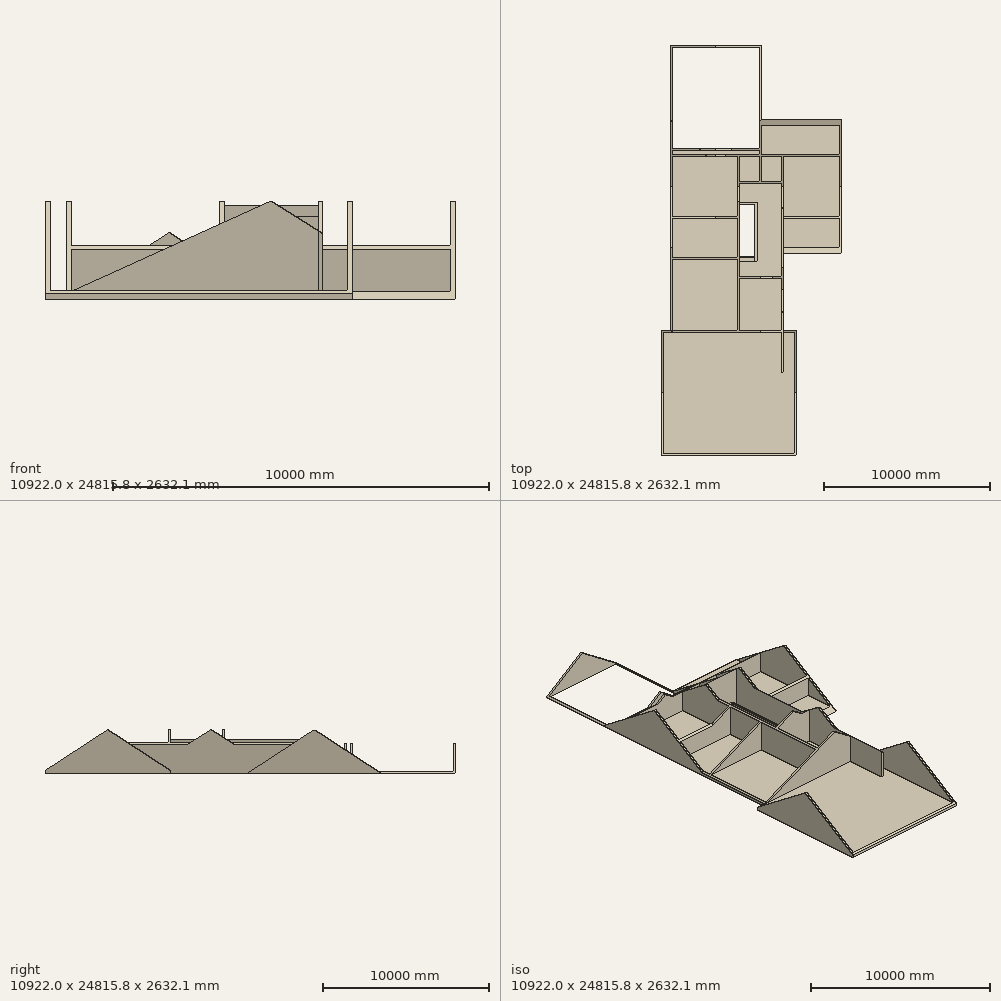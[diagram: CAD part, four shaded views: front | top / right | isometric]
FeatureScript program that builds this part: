
annotation { "Feature Type Name" : "Feature", "Feature Type Description" : "" }
export const myFeature = defineFeature(function(context is Context, id is Id, definition is map)
    precondition{}
    {
        {
            var Q0;
            Q0=qCreatedBy(makeId("Top.planeOp"),FACE);
            var sketch = newSketch(context, id + "F0", { "sketchPlane" : qUnion([Q0])});
            skLineSegment(sketch, "E0", {"start": v(0, 0) * mm, "end": v(8178.8, 0) * mm});
            skLineSegment(sketch, "E1", {"start": v(0, 0) * mm, "end": v(0, 7569.2) * mm});
            skLineSegment(sketch, "E2", {"start": v(0, 7569.2) * mm, "end": v(558.8, 7569.2) * mm});
            skLineSegment(sketch, "E3", {"start": v(558.8, 7569.2) * mm, "end": v(558.8, 24815.8) * mm});
            skLineSegment(sketch, "E4", {"start": v(558.8, 24815.8) * mm, "end": v(6045.2, 24815.8) * mm});
            skLineSegment(sketch, "E5", {"start": v(6045.2, 24815.8) * mm, "end": v(6045.2, 20548.6) * mm});
            skLineSegment(sketch, "E6", {"start": v(6045.2, 20548.6) * mm, "end": v(10922, 20548.6) * mm});
            skLineSegment(sketch, "E7", {"start": v(10922, 20548.6) * mm, "end": v(10922, 12014.2) * mm});
            skLineSegment(sketch, "E8", {"start": v(10922, 12014.2) * mm, "end": v(7391.4, 12014.2) * mm});
            skLineSegment(sketch, "E9", {"start": v(7391.4, 12014.2) * mm, "end": v(7391.4, 7569.2) * mm});
            skLineSegment(sketch, "E10", {"start": v(7391.4, 7569.2) * mm, "end": v(8178.8, 7569.2) * mm});
            skLineSegment(sketch, "E11", {"start": v(8178.8, 7569.2) * mm, "end": v(8178.8, 0) * mm});
            skSolve(sketch);
        }
        {
            var Q0;
            Q0 = qSketchRegion(id + "F0", true);
            extrude(context, id + "F1", {"entities" : qUnion([Q0]), "depth" : 2632.07 * mm});
        }
        {
            var Q0;
            Q0=makeQuery(id+"F1.opExtrude","SWEPT_FACE",FACE,{"disambiguationData":[OSD([sQuery(id+"F0.wireOp",EDGE,"E7")])]});
            var sketch = newSketch(context, id + "F2", { "sketchPlane" : qUnion([Q0])});
            skLineSegment(sketch, "E12", {"start": v(16281.4, 2632.08) * mm, "end": v(16281.4, 219.08) * mm, "construction": true});
            skLineSegment(sketch, "E13", {"start": v(14452.6, 219.08) * mm, "end": v(18110.2, 219.08) * mm, "construction": true});
            skLineSegment(sketch, "E14", {"start": v(14452.6, 219.08) * mm, "end": v(14452.6, 1438.28) * mm, "construction": true});
            skLineSegment(sketch, "E15", {"start": v(16281.4, 2632.08) * mm, "end": v(12249.29, 0) * mm});
            skLineSegment(sketch, "E16", {"start": v(12249.29, 0) * mm, "end": v(12014.2, 0) * mm});
            skLineSegment(sketch, "E17", {"start": v(12014.2, 0) * mm, "end": v(12014.2, 2632.08) * mm});
            skLineSegment(sketch, "E18", {"start": v(12014.2, 2632.08) * mm, "end": v(16281.4, 2632.08) * mm});
            skLineSegment(sketch, "E19.MirrorCS", {"start": v(16281.4, 2632.08) * mm, "end": v(20313.51, 0) * mm});
            skLineSegment(sketch, "E20.MirrorCS", {"start": v(20313.51, 0) * mm, "end": v(20548.6, 0) * mm});
            skLineSegment(sketch, "E21.MirrorCS", {"start": v(20548.6, 0) * mm, "end": v(20548.6, 2632.08) * mm});
            skLineSegment(sketch, "E22.MirrorCS", {"start": v(20548.6, 2632.08) * mm, "end": v(16281.4, 2632.08) * mm});
            skLineSegment(sketch, "E23", {"start": v(3784.6, 2632.08) * mm, "end": v(3784.6, 219.08) * mm, "construction": true});
            skLineSegment(sketch, "E24", {"start": v(1955.8, 219.08) * mm, "end": v(5613.4, 219.08) * mm, "construction": true});
            skLineSegment(sketch, "E25", {"start": v(1955.8, 219.08) * mm, "end": v(1955.8, 1438.28) * mm, "construction": true});
            skLineSegment(sketch, "E26", {"start": v(3784.6, 2632.08) * mm, "end": v(0, 161.57) * mm});
            skLineSegment(sketch, "E27", {"start": v(0, 161.57) * mm, "end": v(0, 2632.08) * mm});
            skLineSegment(sketch, "E28", {"start": v(0, 2632.08) * mm, "end": v(3784.6, 2632.08) * mm});
            skLineSegment(sketch, "E29.MirrorCS", {"start": v(3784.6, 2632.08) * mm, "end": v(7569.2, 161.57) * mm});
            skLineSegment(sketch, "E30.MirrorCS", {"start": v(7569.2, 161.57) * mm, "end": v(7569.2, 2632.08) * mm});
            skLineSegment(sketch, "E31.MirrorCS", {"start": v(7569.2, 2632.08) * mm, "end": v(3784.6, 2632.08) * mm});
            skSolve(sketch);
        }
        {
            var Q0;
            Q0 = qSketchRegion(id + "F2", true);
            var Q1;
            Q1=makeQuery(id+"F1.opExtrude","SWEPT_FACE",FACE,{"disambiguationData":[OSD([sQuery(id+"F0.wireOp",EDGE,"E1")])]});
            extrude(context, id + "F3", {"entities" : qUnion([Q0]), "operationType" : NewBodyOperationType.REMOVE, "endBound" : BoundingType.UP_TO_SURFACE, "oppositeDirection" : true, "endBoundEntityFace" : qUnion([Q1]), "depth" : 25.4 * mm});
        }
        {
            var Q0;
            Q0=makeQuery(id+"F3.boolean.opBoolean","COPY",FACE,{"derivedFrom":makeQuery(id+"F3.opExtrude","SWEPT_FACE",FACE,{"disambiguationData":[OSD([sQuery(id+"F2.wireOp",EDGE,"E30.MirrorCS")])]})});
            var sketch = newSketch(context, id + "F4", { "sketchPlane" : qUnion([Q0])});
            skLineSegment(sketch, "E32", {"start": v(6010.27, 2632.07) * mm, "end": v(6010.27, 219.07) * mm, "construction": true});
            skLineSegment(sketch, "E33", {"start": v(4756.15, 219.07) * mm, "end": v(7264.4, 219.07) * mm, "construction": true});
            skLineSegment(sketch, "E34", {"start": v(4756.15, 219.07) * mm, "end": v(4756.15, 1844.67) * mm, "construction": true});
            skLineSegment(sketch, "E35", {"start": v(6010.27, 2632.07) * mm, "end": v(558.8, 161.57) * mm});
            skLineSegment(sketch, "E36", {"start": v(558.8, 161.57) * mm, "end": v(558.8, 2632.07) * mm});
            skLineSegment(sketch, "E37", {"start": v(558.8, 2632.07) * mm, "end": v(6010.27, 2632.07) * mm});
            skLineSegment(sketch, "E38.MirrorCS", {"start": v(7264.4, 219.07) * mm, "end": v(7264.4, 1844.67) * mm, "construction": true});
            skLineSegment(sketch, "E39", {"start": v(6010.27, 2632.07) * mm, "end": v(7391.4, 1764.94) * mm});
            skLineSegment(sketch, "E40", {"start": v(7391.4, 1764.94) * mm, "end": v(7391.4, 2632.07) * mm});
            skLineSegment(sketch, "E41", {"start": v(7391.4, 2632.07) * mm, "end": v(6010.27, 2632.07) * mm});
            skSolve(sketch);
        }
        {
            var Q0;
            Q0 = qSketchRegion(id + "F4", true);
            extrude(context, id + "F5", {"entities" : qUnion([Q0]), "operationType" : NewBodyOperationType.REMOVE, "endBound" : BoundingType.UP_TO_NEXT, "oppositeDirection" : true, "depth" : 25.4 * mm});
        }
        {
            var Q0;
            Q0=makeQuery(id+"F3.boolean.opBoolean","COPY",FACE,{"derivedFrom":makeQuery(id+"F3.opExtrude","SWEPT_FACE",FACE,{"disambiguationData":[OSD([sQuery(id+"F2.wireOp",EDGE,"E30.MirrorCS")])]})});
            var sketch = newSketch(context, id + "F6", { "sketchPlane" : qUnion([Q0])});
            skLineSegment(sketch, "E42", {"start": v(558.8, 161.57) * mm, "end": v(6010.27, 2632.08) * mm});
            skLineSegment(sketch, "E43", {"start": v(6010.27, 2632.08) * mm, "end": v(7391.4, 1764.94) * mm});
            skLineSegment(sketch, "E44", {"start": v(7391.4, 1764.94) * mm, "end": v(7391.4, 161.57) * mm});
            skLineSegment(sketch, "E45", {"start": v(7391.4, 161.57) * mm, "end": v(558.8, 161.57) * mm});
            skSolve(sketch);
        }
        {
            var Q0;
            Q0 = qSketchRegion(id + "F6", true);
            extrude(context, id + "F7", {"entities" : qUnion([Q0]), "operationType" : NewBodyOperationType.ADD, "endBound" : BoundingType.UP_TO_NEXT, "depth" : 25.4 * mm});
        }
        {
            var Q0;
            Q0=makeQuery(id+"F3.boolean.opBoolean","COPY",FACE,{"derivedFrom":makeQuery(id+"F3.opExtrude","SWEPT_FACE",FACE,{"disambiguationData":[OSD([sQuery(id+"F2.wireOp",EDGE,"E17")])]})});
            var sketch = newSketch(context, id + "F8", { "sketchPlane" : qUnion([Q0])});
            skLineSegment(sketch, "E46", {"start": v(-6010.27, 2632.08) * mm, "end": v(-7391.4, 1764.94) * mm});
            skLineSegment(sketch, "E47", {"start": v(-7391.4, 1764.94) * mm, "end": v(-7391.4, 0) * mm});
            skLineSegment(sketch, "E48", {"start": v(-7391.4, 0) * mm, "end": v(-558.8, 0) * mm});
            skLineSegment(sketch, "E49", {"start": v(-558.8, 161.57) * mm, "end": v(-6010.27, 2632.08) * mm});
            skLineSegment(sketch, "E50", {"start": v(-558.8, 161.57) * mm, "end": v(-558.8, 0) * mm});
            skSolve(sketch);
        }
        {
            var Q0;
            Q0 = qSketchRegion(id + "F8", true);
            extrude(context, id + "F9", {"entities" : qUnion([Q0]), "operationType" : NewBodyOperationType.ADD, "endBound" : BoundingType.UP_TO_NEXT, "depth" : 25.4 * mm});
        }
        {
            var Q0;
            Q0=makeQuery(id+"F1.opExtrude","SWEPT_FACE",FACE,{"disambiguationData":[OSD([sQuery(id+"F0.wireOp",EDGE,"E4")])]});
            var sketch = newSketch(context, id + "F10", { "sketchPlane" : qUnion([Q0])});
            skLineSegment(sketch, "E51", {"start": v(-3302, 2632.08) * mm, "end": v(-3302, 0) * mm, "construction": true});
            skPoint(sketch, "E52", {"position": v(-3302, 219.07) * mm});
            skPoint(sketch, "E53", {"position": v(-3302, 1793.88) * mm});
            skLineSegment(sketch, "E54", {"start": v(-5130.8, 219.07) * mm, "end": v(-1473.2, 219.07) * mm, "construction": true});
            skLineSegment(sketch, "E55", {"start": v(-5130.8, 219.08) * mm, "end": v(-5130.8, 1438.27) * mm, "construction": true});
            skLineSegment(sketch, "E56", {"start": v(-5130.8, 1438.27) * mm, "end": v(-3302, 2632.08) * mm, "construction": true});
            skLineSegment(sketch, "E57", {"start": v(-3302, 1793.88) * mm, "end": v(-6045.2, 3.17) * mm});
            skLineSegment(sketch, "E58", {"start": v(-6045.2, 3.17) * mm, "end": v(-6045.2, 2632.08) * mm});
            skLineSegment(sketch, "E59", {"start": v(-6045.2, 2632.08) * mm, "end": v(-3302, 2632.08) * mm});
            skLineSegment(sketch, "E60.MirrorCS", {"start": v(-3302, 1793.88) * mm, "end": v(-558.8, 3.17) * mm});
            skLineSegment(sketch, "E61.MirrorCS", {"start": v(-558.8, 3.17) * mm, "end": v(-558.8, 2632.08) * mm});
            skLineSegment(sketch, "E62.MirrorCS", {"start": v(-558.8, 2632.08) * mm, "end": v(-3302, 2632.08) * mm});
            skSolve(sketch);
        }
        {
            var Q0;
            Q0 = qSketchRegion(id + "F10", true);
            extrude(context, id + "F11", {"entities" : qUnion([Q0]), "operationType" : NewBodyOperationType.REMOVE, "endBound" : BoundingType.UP_TO_NEXT, "oppositeDirection" : true, "depth" : 25.4 * mm});
        }
        {
            var Q0;
            Q0=makeQuery(id+"F3.boolean.opBoolean","COPY",FACE,{"derivedFrom":makeQuery(id+"F3.opExtrude","SWEPT_FACE",FACE,{"disambiguationData":[OSD([sQuery(id+"F2.wireOp",EDGE,"E21.MirrorCS")])]})});
            var sketch = newSketch(context, id + "F12", { "sketchPlane" : qUnion([Q0])});
            skLineSegment(sketch, "E63", {"start": v(3302, 1793.88) * mm, "end": v(558.8, 3.17) * mm});
            skLineSegment(sketch, "E64", {"start": v(558.8, 3.17) * mm, "end": v(558.8, 0) * mm});
            skLineSegment(sketch, "E65", {"start": v(558.8, 0) * mm, "end": v(6045.2, 0) * mm});
            skLineSegment(sketch, "E66", {"start": v(6045.2, 0) * mm, "end": v(6045.2, 3.17) * mm});
            skLineSegment(sketch, "E67", {"start": v(6045.2, 3.17) * mm, "end": v(3302, 1793.88) * mm});
            skSolve(sketch);
        }
        {
            var Q0;
            Q0 = qSketchRegion(id + "F12", true);
            extrude(context, id + "F13", {"entities" : qUnion([Q0]), "operationType" : NewBodyOperationType.ADD, "endBound" : BoundingType.UP_TO_NEXT, "depth" : 25.4 * mm});
        }
        {
            var Q0;
            Q0=makeQuery(id+"F9.boolean.opBoolean","MERGE",FACE,{"derivedFrom":[makeQuery(id+"F7.boolean.opBoolean","MERGE",FACE,{"derivedFrom":[makeQuery(id+"F1.opExtrude","SWEPT_FACE",FACE,{"disambiguationData":[OSD([sQuery(id+"F0.wireOp",EDGE,"E9")])]}),makeQuery(id+"F7.opExtrude","SWEPT_FACE",FACE,{"disambiguationData":[OSD([sQuery(id+"F6.wireOp",EDGE,"E44")])]})]}),makeQuery(id+"F9.opExtrude","SWEPT_FACE",FACE,{"disambiguationData":[OSD([sQuery(id+"F8.wireOp",EDGE,"E47")])]})]});
            var sketch = newSketch(context, id + "F14", { "sketchPlane" : qUnion([Q0])});
            skLineSegment(sketch, "E68", {"start": v(3784.6, 2632.08) * mm, "end": v(16281.4, 2632.08) * mm, "construction": true});
            skLineSegment(sketch, "E69", {"start": v(10033, 2632.08) * mm, "end": v(10033, 0) * mm, "construction": true});
            skLineSegment(sketch, "E70", {"start": v(8778.88, 219.08) * mm, "end": v(11287.13, 219.08) * mm, "construction": true});
            skPoint(sketch, "E71", {"position": v(10033, 219.08) * mm});
            skLineSegment(sketch, "E72", {"start": v(8778.88, 219.08) * mm, "end": v(8778.88, 1844.68) * mm, "construction": true});
            skLineSegment(sketch, "E73", {"start": v(10033, 2632.07) * mm, "end": v(8651.87, 1764.94) * mm});
            skLineSegment(sketch, "E74.MirrorCS", {"start": v(10033, 2632.07) * mm, "end": v(11414.13, 1764.94) * mm});
            skLineSegment(sketch, "E75", {"start": v(8651.87, 1764.94) * mm, "end": v(11414.13, 1764.94) * mm});
            skSolve(sketch);
        }
        {
            var Q0;
            Q0 = qSketchRegion(id + "F14", true);
            extrude(context, id + "F15", {"entities" : qUnion([Q0]), "operationType" : NewBodyOperationType.ADD, "endBound" : BoundingType.UP_TO_NEXT, "oppositeDirection" : true, "depth" : 25.4 * mm});
        }
        {
            var Q0;
            Q0=qCreatedBy(makeId("Top.planeOp"),FACE);
            cPlane(context, id + "F16", {"entities" : qUnion([Q0]), "cplaneType" : CPlaneType.OFFSET, "offset" : 2632.07 * mm, "width" : 152.4 * mm, "height" : 152.4 * mm});
        }
        {
            var Q0;
            Q0=qCreatedBy(id+"F16.planeOp",FACE);
            var sketch = newSketch(context, id + "F17", { "sketchPlane" : qUnion([Q0])});
            skLineSegment(sketch, "E76.bottom", {"start": v(685.8, 24688.8) * mm, "end": v(5918.2, 24688.8) * mm});
            skLineSegment(sketch, "E76.top", {"start": v(685.8, 18592.8) * mm, "end": v(5918.2, 18592.8) * mm});
            skLineSegment(sketch, "E76.left", {"start": v(685.8, 24688.8) * mm, "end": v(685.8, 18592.8) * mm});
            skLineSegment(sketch, "E76.right", {"start": v(5918.2, 24688.8) * mm, "end": v(5918.2, 18592.8) * mm});
            skSolve(sketch);
        }
        {
            var Q0;
            Q0 = qSketchRegion(id + "F17", true);
            extrude(context, id + "F18", {"entities" : qUnion([Q0]), "operationType" : NewBodyOperationType.REMOVE, "endBound" : BoundingType.THROUGH_ALL, "oppositeDirection" : true, "depth" : 25.4 * mm});
        }
        {
            var Q0;
            Q0=qCreatedBy(id+"F16.planeOp",FACE);
            var sketch = newSketch(context, id + "F19", { "sketchPlane" : qUnion([Q0])});
            skLineSegment(sketch, "E77.bottom", {"start": v(7391.4, 18110.2) * mm, "end": v(10795, 18110.2) * mm});
            skLineSegment(sketch, "E77.top", {"start": v(7391.4, 14452.6) * mm, "end": v(10795, 14452.6) * mm});
            skLineSegment(sketch, "E77.left", {"start": v(7391.4, 18110.2) * mm, "end": v(7391.4, 14452.6) * mm});
            skLineSegment(sketch, "E77.right", {"start": v(10795, 18110.2) * mm, "end": v(10795, 14452.6) * mm});
            skLineSegment(sketch, "E78", {"start": v(10922, 16281.4) * mm, "end": v(558.8, 16281.4) * mm, "construction": true});
            skPoint(sketch, "E79", {"position": v(10795, 16281.4) * mm});
            skLineSegment(sketch, "E80.bottom", {"start": v(685.8, 18110.2) * mm, "end": v(4629.15, 18110.2) * mm});
            skLineSegment(sketch, "E80.top", {"start": v(685.8, 14452.6) * mm, "end": v(4629.15, 14452.6) * mm});
            skLineSegment(sketch, "E80.left", {"start": v(685.8, 18110.2) * mm, "end": v(685.8, 14452.6) * mm});
            skLineSegment(sketch, "E80.right", {"start": v(4629.15, 18110.2) * mm, "end": v(4629.15, 14452.6) * mm});
            skLineSegment(sketch, "E81.bottom", {"start": v(4756.15, 18110.2) * mm, "end": v(5946.77, 18110.2) * mm});
            skLineSegment(sketch, "E81.top", {"start": v(4756.15, 16586.2) * mm, "end": v(5946.77, 16586.2) * mm});
            skLineSegment(sketch, "E81.left", {"start": v(4756.15, 18110.2) * mm, "end": v(4756.15, 16586.2) * mm});
            skLineSegment(sketch, "E81.right", {"start": v(5946.77, 18110.2) * mm, "end": v(5946.77, 16586.2) * mm});
            skLineSegment(sketch, "E82.bottom", {"start": v(7264.4, 18110.2) * mm, "end": v(6073.77, 18110.2) * mm});
            skLineSegment(sketch, "E82.top", {"start": v(7264.4, 16586.2) * mm, "end": v(6073.77, 16586.2) * mm});
            skLineSegment(sketch, "E82.left", {"start": v(7264.4, 18110.2) * mm, "end": v(7264.4, 16586.2) * mm});
            skLineSegment(sketch, "E82.right", {"start": v(6073.77, 18110.2) * mm, "end": v(6073.77, 16586.2) * mm});
            skLineSegment(sketch, "E83.bottom", {"start": v(10795, 14325.6) * mm, "end": v(7391.4, 14325.6) * mm});
            skLineSegment(sketch, "E83.top", {"start": v(10795, 12014.2) * mm, "end": v(7391.4, 12014.2) * mm});
            skLineSegment(sketch, "E83.left", {"start": v(10795, 14325.6) * mm, "end": v(10795, 12014.2) * mm});
            skLineSegment(sketch, "E83.right", {"start": v(7391.4, 14325.6) * mm, "end": v(7391.4, 12014.2) * mm});
            skLineSegment(sketch, "E84.bottom", {"start": v(10795, 18237.2) * mm, "end": v(6045.2, 18237.2) * mm});
            skLineSegment(sketch, "E84.top", {"start": v(10795, 20548.6) * mm, "end": v(6045.2, 20548.6) * mm});
            skLineSegment(sketch, "E84.left", {"start": v(10795, 18237.2) * mm, "end": v(10795, 20548.6) * mm});
            skLineSegment(sketch, "E84.right", {"start": v(6045.2, 18237.2) * mm, "end": v(6045.2, 20548.6) * mm});
            skLineSegment(sketch, "E85.bottom", {"start": v(685.8, 18237.2) * mm, "end": v(5918.2, 18237.2) * mm});
            skLineSegment(sketch, "E85.top", {"start": v(685.8, 18465.8) * mm, "end": v(5918.2, 18465.8) * mm});
            skLineSegment(sketch, "E85.left", {"start": v(685.8, 18237.2) * mm, "end": v(685.8, 18465.8) * mm});
            skLineSegment(sketch, "E85.right", {"start": v(5918.2, 18237.2) * mm, "end": v(5918.2, 18465.8) * mm});
            skLineSegment(sketch, "E86.bottom", {"start": v(685.8, 14325.6) * mm, "end": v(4629.15, 14325.6) * mm});
            skLineSegment(sketch, "E86.top", {"start": v(685.8, 12014.2) * mm, "end": v(4629.15, 12014.2) * mm});
            skLineSegment(sketch, "E86.left", {"start": v(685.8, 14325.6) * mm, "end": v(685.8, 12014.2) * mm});
            skLineSegment(sketch, "E86.right", {"start": v(4629.15, 14325.6) * mm, "end": v(4629.15, 12014.2) * mm});
            skLineSegment(sketch, "E87.bottom", {"start": v(127, 7442.2) * mm, "end": v(8051.8, 7442.2) * mm});
            skLineSegment(sketch, "E87.top", {"start": v(127, 127) * mm, "end": v(8051.8, 127) * mm});
            skLineSegment(sketch, "E87.left", {"start": v(127, 7442.2) * mm, "end": v(127, 127) * mm});
            skLineSegment(sketch, "E87.right", {"start": v(8051.8, 7442.2) * mm, "end": v(8051.8, 127) * mm});
            skLineSegment(sketch, "E88.bottom", {"start": v(685.8, 11887.2) * mm, "end": v(4629.15, 11887.2) * mm});
            skLineSegment(sketch, "E88.top", {"start": v(685.8, 7569.2) * mm, "end": v(4629.15, 7569.2) * mm});
            skLineSegment(sketch, "E88.left", {"start": v(685.8, 11887.2) * mm, "end": v(685.8, 7569.2) * mm});
            skLineSegment(sketch, "E88.right", {"start": v(4629.15, 11887.2) * mm, "end": v(4629.15, 7569.2) * mm});
            skLineSegment(sketch, "E89.bottom", {"start": v(4756.15, 16459.2) * mm, "end": v(7264.4, 16459.2) * mm});
            skLineSegment(sketch, "E89.top", {"start": v(4756.15, 10820.4) * mm, "end": v(7264.4, 10820.4) * mm});
            skLineSegment(sketch, "E89.left", {"start": v(4756.15, 16459.2) * mm, "end": v(4756.15, 10820.4) * mm});
            skLineSegment(sketch, "E89.right", {"start": v(7264.4, 16459.2) * mm, "end": v(7264.4, 10820.4) * mm});
            skLineSegment(sketch, "E90.bottom", {"start": v(4756.15, 10693.4) * mm, "end": v(7264.4, 10693.4) * mm});
            skLineSegment(sketch, "E90.top", {"start": v(4756.15, 7569.2) * mm, "end": v(7264.4, 7569.2) * mm});
            skLineSegment(sketch, "E90.left", {"start": v(4756.15, 10693.4) * mm, "end": v(4756.15, 7569.2) * mm});
            skLineSegment(sketch, "E90.right", {"start": v(7264.4, 10693.4) * mm, "end": v(7264.4, 7569.2) * mm});
            skSolve(sketch);
        }
        {
            var Q0;
            Q0 = qSketchRegion(id + "F19", true);
            extrude(context, id + "F20", {"entities" : qUnion([Q0]), "operationType" : NewBodyOperationType.REMOVE, "oppositeDirection" : true, "depth" : 2413 * mm});
        }
        {
            var Q0;
            Q0=makeQuery(id+"F20.boolean.opBoolean","COPY",FACE,{"derivedFrom":makeQuery(id+"F20.opExtrude","CAP_FACE",FACE,{"disambiguationData":[OSD([sQuery(id+"F19.wireOp",EDGE,"E89.bottom"),sQuery(id+"F19.wireOp",EDGE,"E89.top"),sQuery(id+"F19.wireOp",EDGE,"E89.left"),sQuery(id+"F19.wireOp",EDGE,"E89.right")])],"isStart":false})});
            var sketch = newSketch(context, id + "F21", { "sketchPlane" : qUnion([Q0])});
            skLineSegment(sketch, "E91.bottom", {"start": v(4756.15, 15214.6) * mm, "end": v(5670.55, 15214.6) * mm});
            skLineSegment(sketch, "E91.top", {"start": v(4756.15, 11734.8) * mm, "end": v(5670.55, 11734.8) * mm});
            skLineSegment(sketch, "E91.left", {"start": v(4756.15, 15214.6) * mm, "end": v(4756.15, 11734.8) * mm});
            skLineSegment(sketch, "E91.right", {"start": v(5670.55, 15214.6) * mm, "end": v(5670.55, 11734.8) * mm});
            skSolve(sketch);
        }
        {
            var Q0;
            Q0 = qSketchRegion(id + "F21", true);
            extrude(context, id + "F22", {"entities" : qUnion([Q0]), "operationType" : NewBodyOperationType.REMOVE, "endBound" : BoundingType.THROUGH_ALL, "oppositeDirection" : true, "depth" : 25.4 * mm});
        }
        {
            var Q0;
            Q0=makeQuery(id+"F22.boolean.opBoolean","MERGE",FACE,{"derivedFrom":[makeQuery(id+"F20.boolean.opBoolean","COPY",FACE,{"derivedFrom":makeQuery(id+"F20.opExtrude","SWEPT_FACE",FACE,{"disambiguationData":[OSD([sQuery(id+"F19.wireOp",EDGE,"E89.left")])]})}),makeQuery(id+"F22.opExtrude","SWEPT_FACE",FACE,{"disambiguationData":[OSD([sQuery(id+"F21.wireOp",EDGE,"E91.left")])]})]});
            var sketch = newSketch(context, id + "F23", { "sketchPlane" : qUnion([Q0])});
            skLineSegment(sketch, "E92.bottom", {"start": v(11734.8, 28.57) * mm, "end": v(12014.2, 28.57) * mm});
            skLineSegment(sketch, "E92.top", {"start": v(11734.8, 0) * mm, "end": v(12014.2, 0) * mm});
            skLineSegment(sketch, "E92.left", {"start": v(11734.8, 28.58) * mm, "end": v(11734.8, 0) * mm});
            skLineSegment(sketch, "E92.right", {"start": v(12014.2, 28.57) * mm, "end": v(12014.2, 0) * mm});
            skSolve(sketch);
        }
        {
            var Q0;
            Q0 = qSketchRegion(id + "F23", true);
            extrude(context, id + "F24", {"entities" : qUnion([Q0]), "operationType" : NewBodyOperationType.ADD, "endBound" : BoundingType.UP_TO_NEXT, "depth" : 25.4 * mm});
        }
        {
            var Q0;
            Q0=makeQuery(id+"F20.boolean.opBoolean","COPY",FACE,{"derivedFrom":makeQuery(id+"F20.opExtrude","CAP_FACE",FACE,{"disambiguationData":[OSD([sQuery(id+"F19.wireOp",EDGE,"E89.bottom"),sQuery(id+"F19.wireOp",EDGE,"E89.top"),sQuery(id+"F19.wireOp",EDGE,"E89.left"),sQuery(id+"F19.wireOp",EDGE,"E89.right")])],"isStart":false})});
            var sketch = newSketch(context, id + "F25", { "sketchPlane" : qUnion([Q0])});
            skLineSegment(sketch, "E93", {"start": v(4756.15, 15214.6) * mm, "end": v(4756.15, 15341.6) * mm});
            skLineSegment(sketch, "E94", {"start": v(4756.15, 15341.6) * mm, "end": v(5797.55, 15341.6) * mm});
            skLineSegment(sketch, "E95", {"start": v(5797.55, 15341.6) * mm, "end": v(5797.55, 11734.8) * mm});
            skLineSegment(sketch, "E96", {"start": v(5797.55, 11734.8) * mm, "end": v(5670.55, 11734.8) * mm});
            skLineSegment(sketch, "E97", {"start": v(5670.55, 11734.8) * mm, "end": v(5670.55, 15214.6) * mm});
            skLineSegment(sketch, "E98", {"start": v(5670.55, 15214.6) * mm, "end": v(4756.15, 15214.6) * mm});
            skSolve(sketch);
        }
        {
            var Q0;
            Q0 = qSketchRegion(id + "F25", true);
            extrude(context, id + "F26", {"entities" : qUnion([Q0]), "operationType" : NewBodyOperationType.ADD, "depth" : 1219.2 * mm});
        }
        {
            var Q0;
            Q0=makeQuery(id+"F20.boolean.opBoolean","COPY",FACE,{"derivedFrom":makeQuery(id+"F20.opExtrude","SWEPT_FACE",FACE,{"disambiguationData":[OSD([sQuery(id+"F19.wireOp",EDGE,"E87.bottom")])]})});
            var sketch = newSketch(context, id + "F27", { "sketchPlane" : qUnion([Q0])});
            skLineSegment(sketch, "E99", {"start": v(7391.4, 1764.94) * mm, "end": v(7264.4, 1844.67) * mm});
            skLineSegment(sketch, "E100", {"start": v(7264.4, 1844.67) * mm, "end": v(7264.4, 219.08) * mm});
            skLineSegment(sketch, "E101", {"start": v(7264.4, 219.08) * mm, "end": v(7391.4, 219.08) * mm});
            skLineSegment(sketch, "E102", {"start": v(7391.4, 219.08) * mm, "end": v(7391.4, 1764.94) * mm});
            skSolve(sketch);
        }
        {
            var Q0;
            Q0 = qSketchRegion(id + "F27", true);
            extrude(context, id + "F28", {"entities" : qUnion([Q0]), "operationType" : NewBodyOperationType.ADD, "depth" : 2438.4 * mm});
        }
    });
